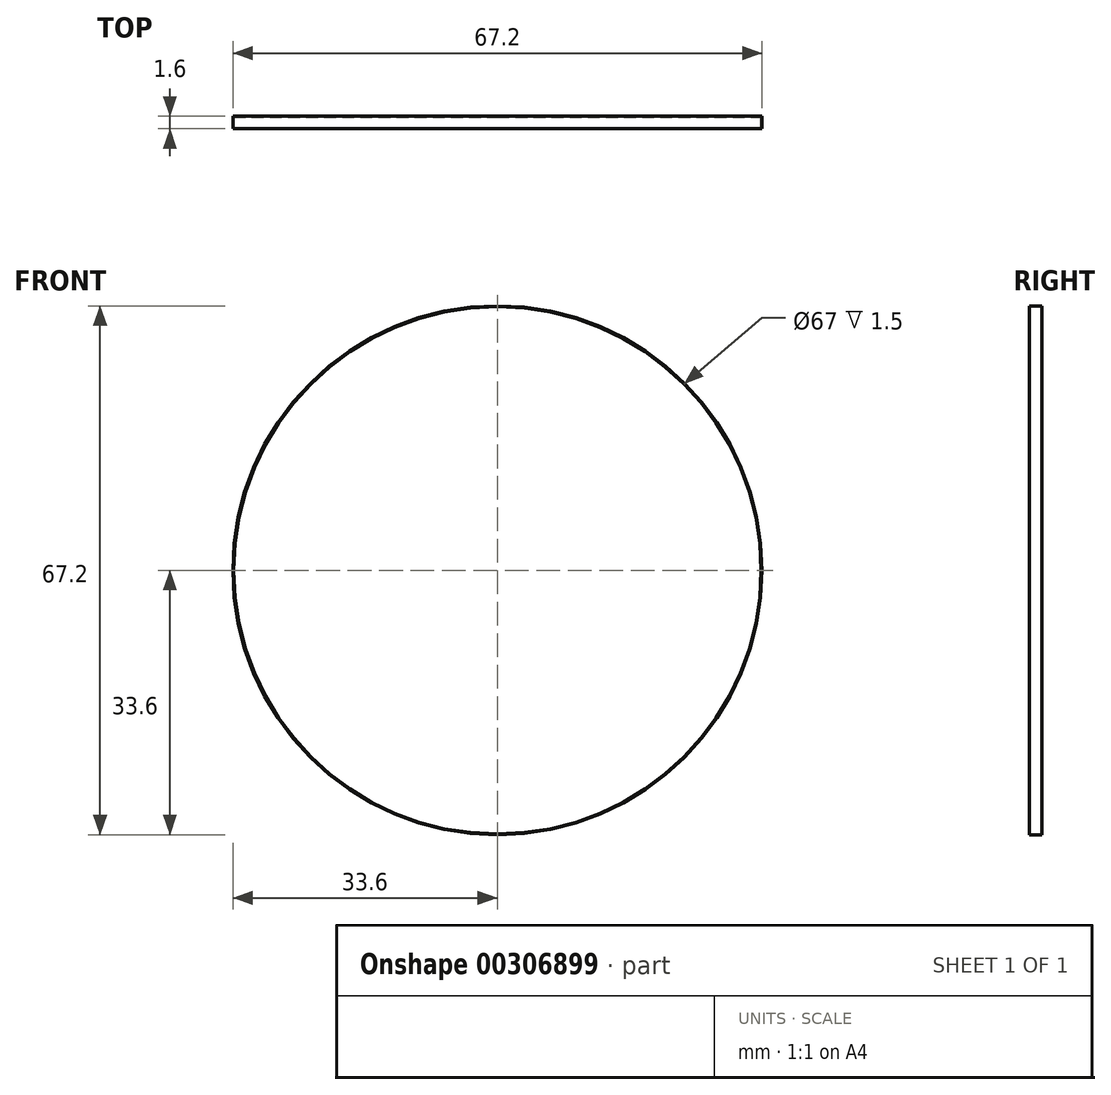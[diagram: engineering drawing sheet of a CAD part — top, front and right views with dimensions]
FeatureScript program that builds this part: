
annotation { "Feature Type Name" : "Feature", "Feature Type Description" : "" }
export const myFeature = defineFeature(function(context is Context, id is Id, definition is map)
    precondition{}
    {
        {
            var Q0;
            Q0=qCreatedBy(makeId("Top.planeOp"),FACE);
            var sketch = newSketch(context, id + "F0", { "sketchPlane" : qUnion([Q0])});
            skLineSegment(sketch, "E0", {"start": v(0, 0) * mm, "end": v(-33.6, 0) * mm});
            skLineSegment(sketch, "E1", {"start": v(-33.6, 0) * mm, "end": v(-33.6, 0.2) * mm});
            skLineSegment(sketch, "E2", {"start": v(-33.6, 0.2) * mm, "end": v(0, 0.2) * mm});
            skLineSegment(sketch, "E3", {"start": v(0, 0.2) * mm, "end": v(0, 0) * mm});
            skLineSegment(sketch, "E4", {"start": v(-33.6, 0) * mm, "end": v(-33.6, -1) * mm});
            skLineSegment(sketch, "E5", {"start": v(-33.6, -1) * mm, "end": v(-33.3, -1) * mm});
            skLineSegment(sketch, "E6", {"start": v(-33.3, -1) * mm, "end": v(-33.3, 0) * mm});
            skLineSegment(sketch, "E7", {"start": v(0, -6.1) * mm, "end": v(-33.6, -6.1) * mm});
            skLineSegment(sketch, "E8", {"start": v(-33.6, -6.1) * mm, "end": v(-33.6, -6) * mm});
            skLineSegment(sketch, "E9", {"start": v(-33.6, -6) * mm, "end": v(0, -6) * mm});
            skLineSegment(sketch, "E10", {"start": v(0, -6) * mm, "end": v(0, -6.1) * mm});
            skLineSegment(sketch, "E11", {"start": v(-33.6, -6.1) * mm, "end": v(-33.6, -7.6) * mm});
            skLineSegment(sketch, "E12", {"start": v(-33.6, -7.6) * mm, "end": v(-33.5, -7.6) * mm});
            skLineSegment(sketch, "E13", {"start": v(-33.5, -7.6) * mm, "end": v(-33.5, -6.1) * mm});
            skSolve(sketch);
        }
        {
            var Q0;
            {var subQ0=sQuery(id+"F0.wireOp",EDGE,"E11");Q0=makeQuery(id+"F0.imprint","IMPRINT",FACE,{"disambiguationData":[TD([[makeQuery(id+"F0.imprint","IMPRINT",EDGE,{"derivedFrom":subQ0}),1.0]])]});}
            var Q1;
            {var subQ0=sQuery(id+"F0.wireOp",EDGE,"E8");Q1=makeQuery(id+"F0.imprint","IMPRINT",FACE,{"disambiguationData":[TD([[makeQuery(id+"F0.imprint","IMPRINT",EDGE,{"derivedFrom":subQ0}),-1.0]])]});}
            var Q2;
            Q2=sQuery(id+"F0.wireOp",EDGE,"E3");
            revolve(context, id + "F1", {"entities" : qUnion([Q0, Q1]), "axis" : qUnion([Q2]), "revolveType" : RevolveType.FULL});
        }
    });
